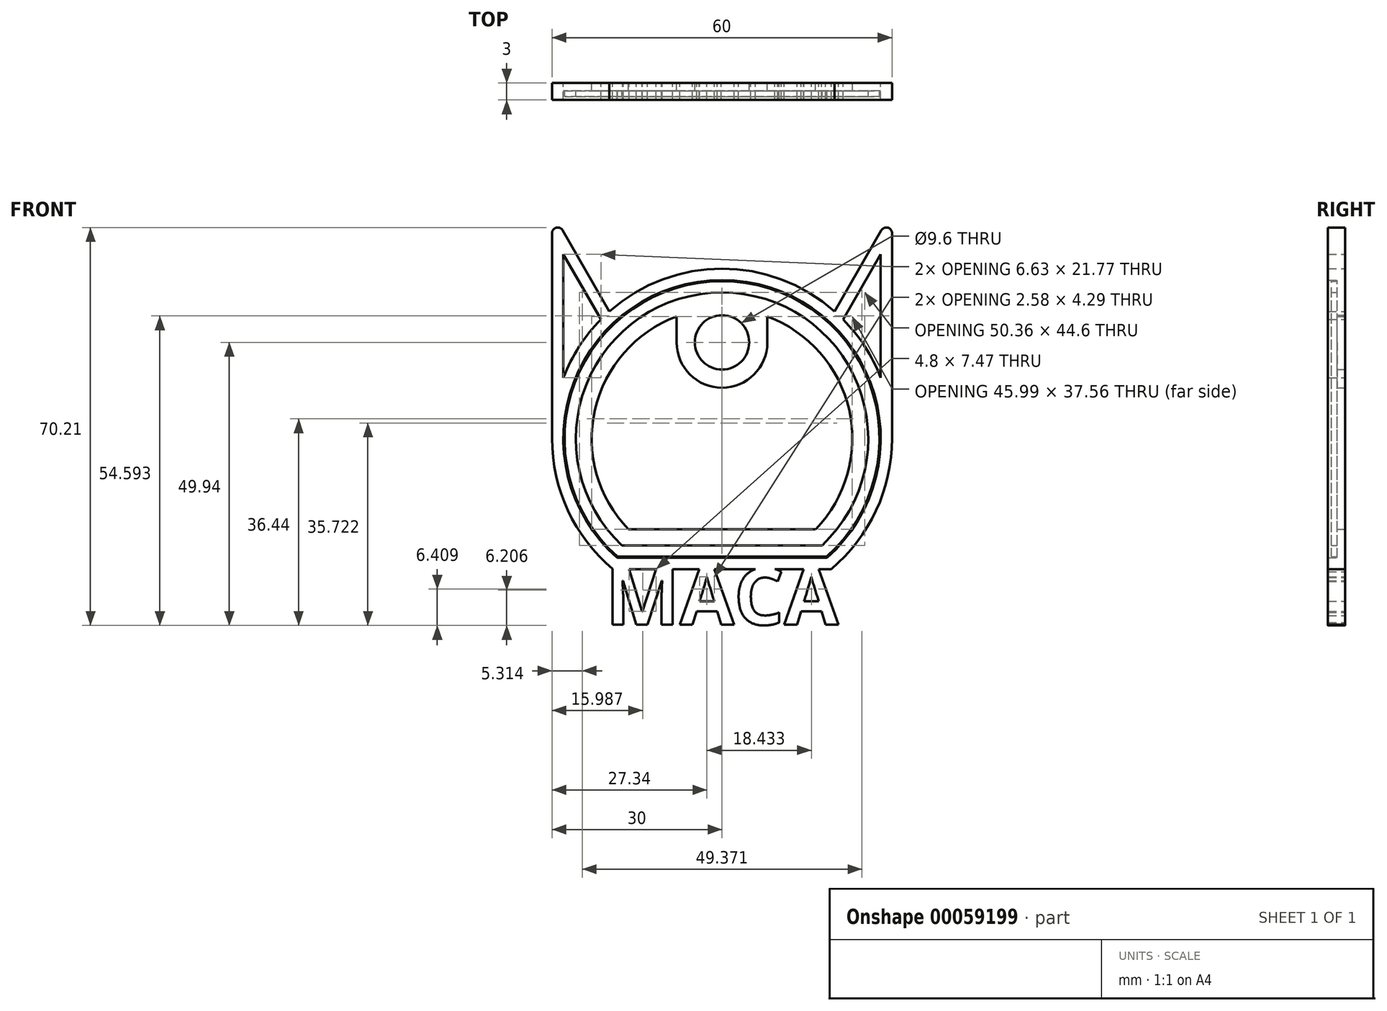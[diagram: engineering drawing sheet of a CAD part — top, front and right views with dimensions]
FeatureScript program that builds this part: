
annotation { "Feature Type Name" : "Feature", "Feature Type Description" : "" }
export const myFeature = defineFeature(function(context is Context, id is Id, definition is map)
    precondition{}
    {
        {
            var Q0;
            Q0=qCreatedBy(makeId("Front.planeOp"),FACE);
            var sketch = newSketch(context, id + "F0", { "sketchPlane" : qUnion([Q0])});
            skArc(sketch, "E0", {"start": v(19.26, -23) * mm, "mid": v(0, 30) * mm, "end": v(-19.26, -23) * mm});
            skLineSegment(sketch, "E1", {"start": v(-30, 0) * mm, "end": v(-30, 36.27) * mm});
            skLineSegment(sketch, "E2", {"start": v(-28.13, 36.77) * mm, "end": v(-19.88, 22.47) * mm});
            skLineSegment(sketch, "E3.MirrorCS", {"start": v(28.13, 36.77) * mm, "end": v(19.88, 22.47) * mm});
            skLineSegment(sketch, "E4.MirrorCS", {"start": v(30, 0) * mm, "end": v(30, 36.27) * mm});
            skLineSegment(sketch, "E5.0", {"start": v(-28, 32.54) * mm, "end": v(-21.37, 21.05) * mm});
            skLineSegment(sketch, "E5.1", {"start": v(-28, 10.77) * mm, "end": v(-28, 32.54) * mm});
            skLineSegment(sketch, "E6.MirrorCS", {"start": v(28, 10.77) * mm, "end": v(28, 32.54) * mm});
            skLineSegment(sketch, "E7.MirrorCS", {"start": v(28, 32.54) * mm, "end": v(21.37, 21.05) * mm});
            skText(sketch, "E8", { "text": "MACA", "fontName": "OpenSans-Bold.ttf"});
            skLineSegment(sketch, "E9", {"start": v(-19.26, -23) * mm, "end": v(19.26, -23) * mm});
            skArc(sketch, "E10.0", {"start": v(18.52, -21) * mm, "mid": v(0, 28) * mm, "end": v(-18.52, -21) * mm});
            skLineSegment(sketch, "E10.1", {"start": v(-18.52, -21) * mm, "end": v(18.52, -21) * mm});
            skCircle(sketch, "E11", {"center": v(0, 17) * mm, "radius": 4.8 * mm});
            skArc(sketch, "E12.0", {"start": v(16.52, -16) * mm, "mid": v(22.43, 5.09) * mm, "end": v(8, 21.56) * mm});
            skLineSegment(sketch, "E12.1", {"start": v(-16.52, -16) * mm, "end": v(16.52, -16) * mm});
            skArc(sketch, "E13.0", {"start": v(-8, 17) * mm, "mid": v(0, 9) * mm, "end": v(8, 17) * mm});
            skLineSegment(sketch, "E14", {"start": v(8, 17) * mm, "end": v(8, 21.56) * mm});
            skLineSegment(sketch, "E15", {"start": v(-8, 17) * mm, "end": v(-8, 21.56) * mm});
            skArc(sketch, "E16.trimOffspring", {"start": v(-8, 21.56) * mm, "mid": v(-22.43, 5.09) * mm, "end": v(-16.52, -16) * mm});
            skPoint(sketch, "E17.visualSharp", {"position": v(-30, 40) * mm});
            skArc(sketch, "E17.filletArc", {"start": v(-28.13, 36.77) * mm, "mid": v(-29.26, 37.23) * mm, "end": v(-30, 36.27) * mm});
            skPoint(sketch, "E18.visualSharp", {"position": v(30, 40) * mm});
            skArc(sketch, "E18.filletArc", {"start": v(30, 36.27) * mm, "mid": v(29.26, 37.23) * mm, "end": v(28.13, 36.77) * mm});
            const initialGuessF0  = {"E8": [-0.02056, -0.0328, 1, 0, 0.01]};
            skSetInitialGuess(sketch, initialGuessF0);
            skSolve(sketch);
        }
        {
            var Q0;
            Q0 = qSketchRegion(id + "F0", true);
            extrude(context, id + "F1", {"entities" : qUnion([Q0]), "depth" : 3 * mm});
        }
        {
            var Q0;
            Q0=makeQuery(id+"F0.imprint","IMPRINT",FACE,{"disambiguationData":[TD([[makeQuery(id+"F0.imprint","IMPRINT",EDGE,{"derivedFrom":sQuery(id+"F0.wireOp",EDGE,"E10.0")}),1.0]])]});
            var Q1;
            Q1=makeQuery(id+"F0.imprint","IMPRINT",FACE,{"disambiguationData":[TD([[makeQuery(id+"F0.imprint","IMPRINT",EDGE,{"derivedFrom":sQuery(id+"F0.wireOp",EDGE,"E11")}),-1.0]])]});
            extrude(context, id + "F2", {"entities" : qUnion([Q0, Q1]), "operationType" : NewBodyOperationType.ADD, "depth" : 1.4 * mm});
        }
        {
            var Q0;
            Q0=makeQuery(id+"F2.opExtrude","CAP_FACE",FACE,{"disambiguationData":[OSD([sQuery(id+"F0.wireOp",EDGE,"E10.0"),sQuery(id+"F0.wireOp",EDGE,"E10.1"),sQuery(id+"F0.wireOp",EDGE,"E11"),sQuery(id+"F0.wireOp",EDGE,"E12.0"),sQuery(id+"F0.wireOp",EDGE,"E12.1"),sQuery(id+"F0.wireOp",EDGE,"E13.0"),sQuery(id+"F0.wireOp",EDGE,"E14"),sQuery(id+"F0.wireOp",EDGE,"E15"),sQuery(id+"F0.wireOp",EDGE,"E16.trimOffspring")])],"isStart":false});
            var sketch = newSketch(context, id + "F3", { "sketchPlane" : qUnion([Q0])});
            skArc(sketch, "E19.0", {"start": v(18.52, -21) * mm, "mid": v(0, 28) * mm, "end": v(-18.52, -21) * mm});
            skLineSegment(sketch, "E19.1", {"start": v(-18.52, -21) * mm, "end": v(18.52, -21) * mm});
            skLineSegment(sketch, "E20.0", {"start": v(-18.44, -20.8) * mm, "end": v(18.44, -20.8) * mm});
            skArc(sketch, "E20.1", {"start": v(18.44, -20.8) * mm, "mid": v(0, 27.8) * mm, "end": v(-18.44, -20.8) * mm});
            skLineSegment(sketch, "E21.0", {"start": v(-17.67, -18.8) * mm, "end": v(17.67, -18.8) * mm});
            skArc(sketch, "E21.1", {"start": v(17.67, -18.8) * mm, "mid": v(0, 25.8) * mm, "end": v(-17.67, -18.8) * mm});
            skSolve(sketch);
        }
        {
            var Q0;
            Q0=makeQuery(id+"F3.imprint","IMPRINT",FACE,{"disambiguationData":[TD([[makeQuery(id+"F3.imprint","IMPRINT",EDGE,{"derivedFrom":sQuery(id+"F3.wireOp",EDGE,"E20.0")}),1.0]])]});
            extrude(context, id + "F4", {"entities" : qUnion([Q0]), "depth" : 1 * mm});
        }
    });
